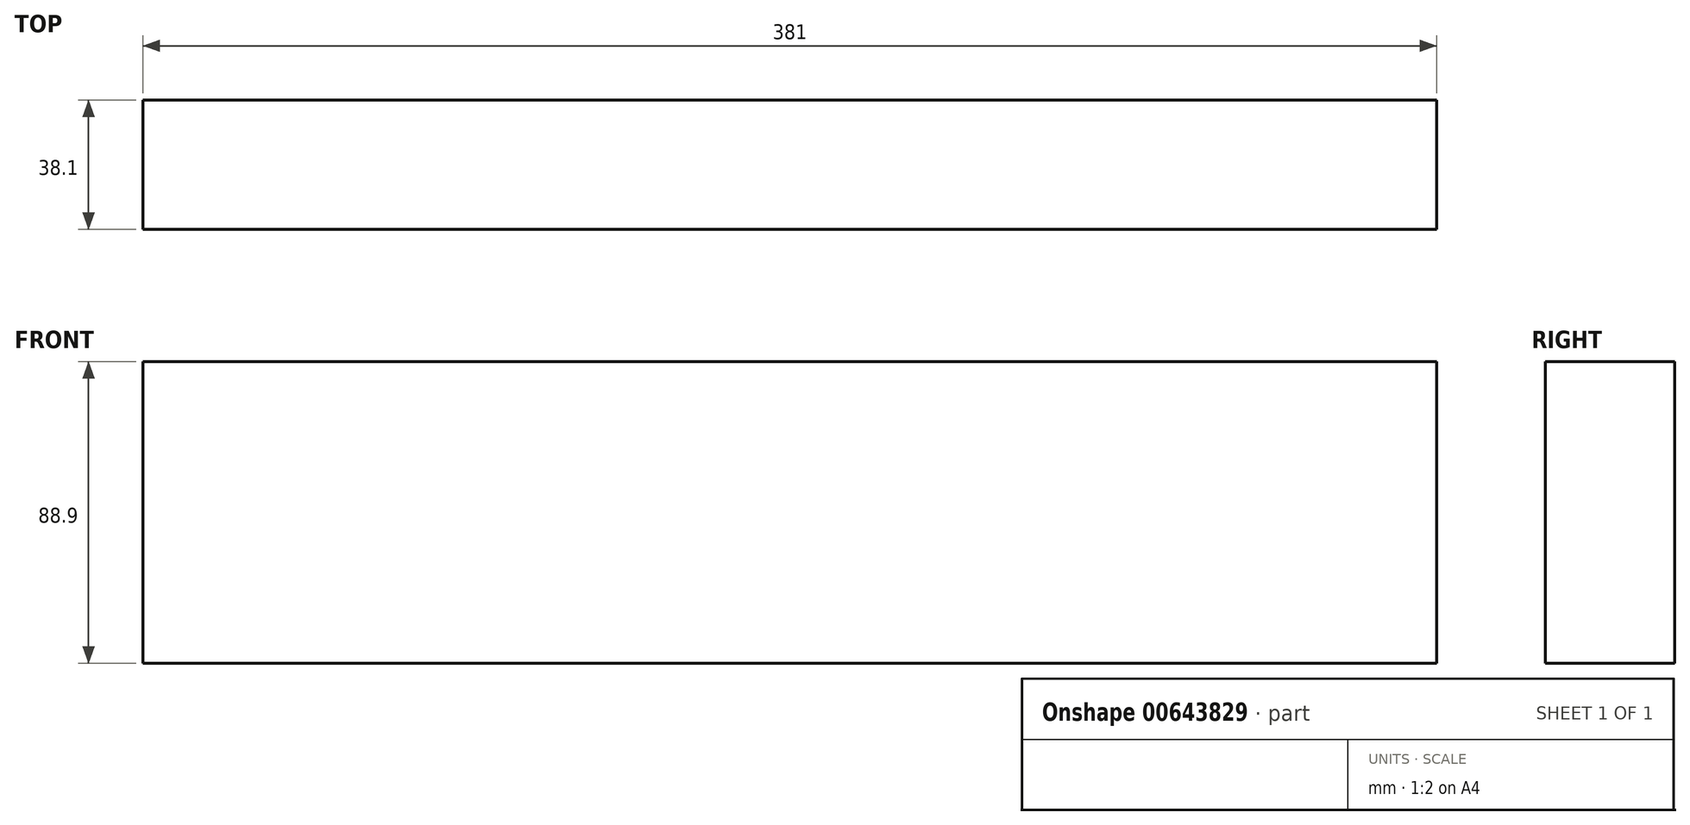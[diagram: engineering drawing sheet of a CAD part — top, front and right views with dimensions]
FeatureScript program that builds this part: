
annotation { "Feature Type Name" : "Feature", "Feature Type Description" : "" }
export const myFeature = defineFeature(function(context is Context, id is Id, definition is map)
    precondition{}
    {
        {
            var Q0;
            Q0=qCreatedBy(makeId("Front.planeOp"),FACE);
            var sketch = newSketch(context, id + "F0", { "sketchPlane" : qUnion([Q0])});
            skLineSegment(sketch, "E0.bottom", {"start": v(30.57, -86.03) * mm, "end": v(-350.43, -86.03) * mm});
            skLineSegment(sketch, "E0.top", {"start": v(30.57, 2.87) * mm, "end": v(-350.43, 2.87) * mm});
            skLineSegment(sketch, "E0.left", {"start": v(30.57, -86.03) * mm, "end": v(30.57, 2.87) * mm});
            skLineSegment(sketch, "E0.right", {"start": v(-350.43, -86.03) * mm, "end": v(-350.43, 2.87) * mm});
            skPoint(sketch, "E0.middle", {"position": v(-159.93, -41.58) * mm});
            skSolve(sketch);
        }
        {
            var Q0;
            Q0 = qSketchRegion(id + "F0", true);
            extrude(context, id + "F1", {"entities" : qUnion([Q0]), "depth" : 38.1 * mm, "offsetDistance" : 25.4 * mm});
        }
    });
